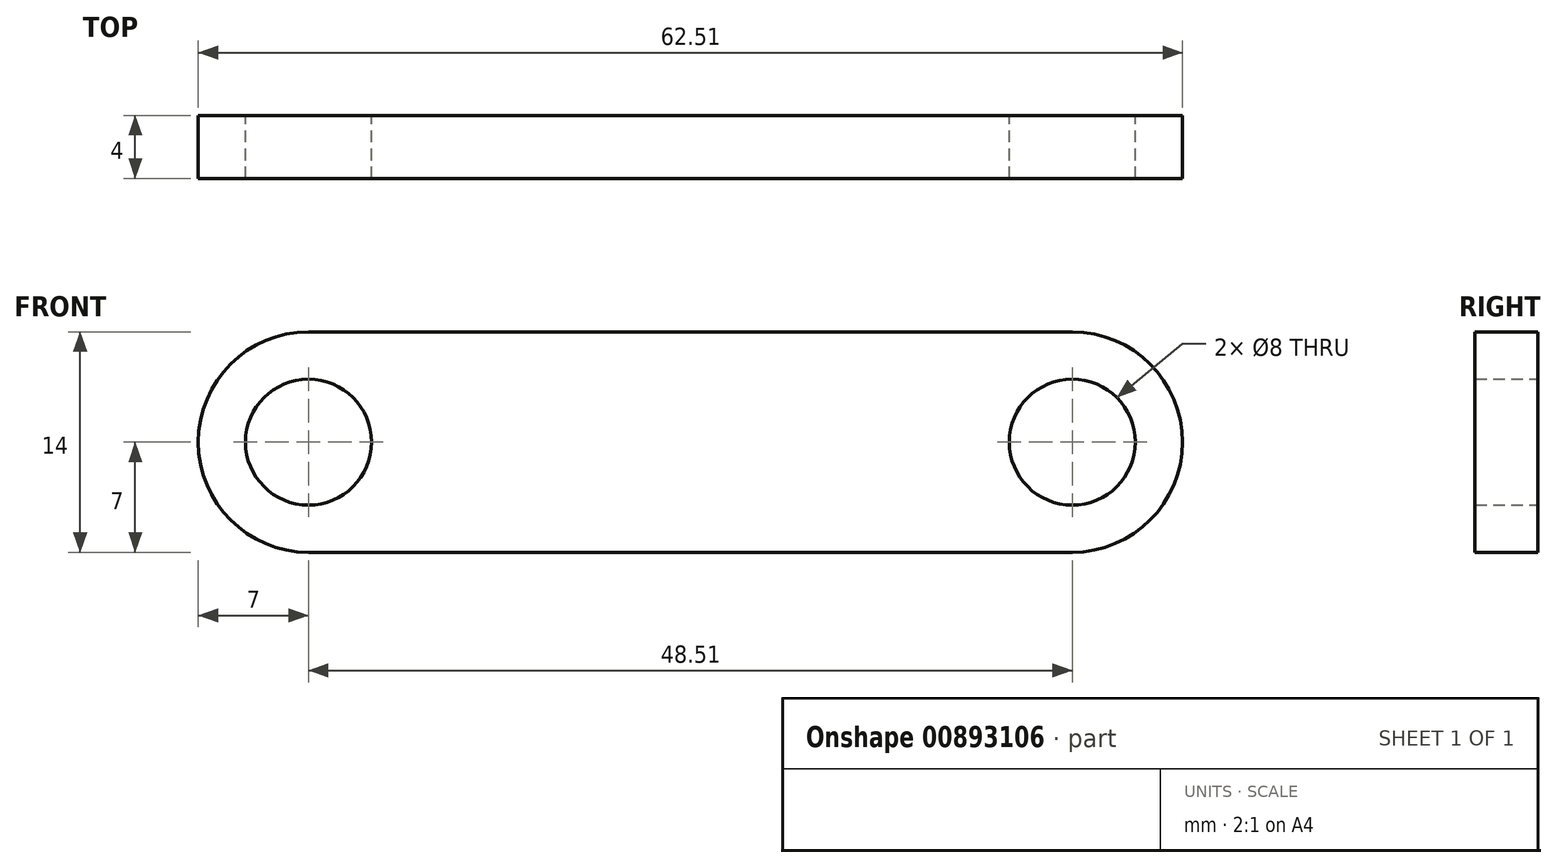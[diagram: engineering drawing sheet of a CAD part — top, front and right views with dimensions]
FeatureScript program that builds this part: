
annotation { "Feature Type Name" : "Feature", "Feature Type Description" : "" }
export const myFeature = defineFeature(function(context is Context, id is Id, definition is map)
    precondition{}
    {
        {
            assignVariable(context, id + "F0", {"name" : "Thickness", "anyValue" : 4});
        }
        {
            var Q0;
            Q0=qCreatedBy(makeId("Front.planeOp"),FACE);
            var sketch = newSketch(context, id + "F1", { "sketchPlane" : qUnion([Q0])});
            skCircle(sketch, "E0", {"center": v(0, 0) * mm, "radius": 4 * mm});
            skCircle(sketch, "E1", {"center": v(48.5, 0) * mm, "radius": 4 * mm});
            skArc(sketch, "E2", {"start": v(48.5, -7) * mm, "mid": v(55.5, 0) * mm, "end": v(48.5, 7) * mm});
            skArc(sketch, "E3", {"start": v(0, 7) * mm, "mid": v(-7, 0) * mm, "end": v(0, -7) * mm});
            skLineSegment(sketch, "E4", {"start": v(0, 7) * mm, "end": v(48.5, 7) * mm});
            skLineSegment(sketch, "E5", {"start": v(0, -7) * mm, "end": v(48.5, -7) * mm});
            skSolve(sketch);
        }
        {
            var Q0;
            Q0=makeQuery(id+"F1.imprint","IMPRINT",FACE,{"disambiguationData":[TD([[makeQuery(id+"F1.imprint","IMPRINT",EDGE,{"derivedFrom":sQuery(id+"F1.wireOp",EDGE,"E0")}),-1.0]])]});
            extrude(context, id + "F2", {"entities" : qUnion([Q0]), "depth" : (getVariable(context, 'Thickness')) * mm, "offsetDistance" : 25 * mm});
        }
    });
